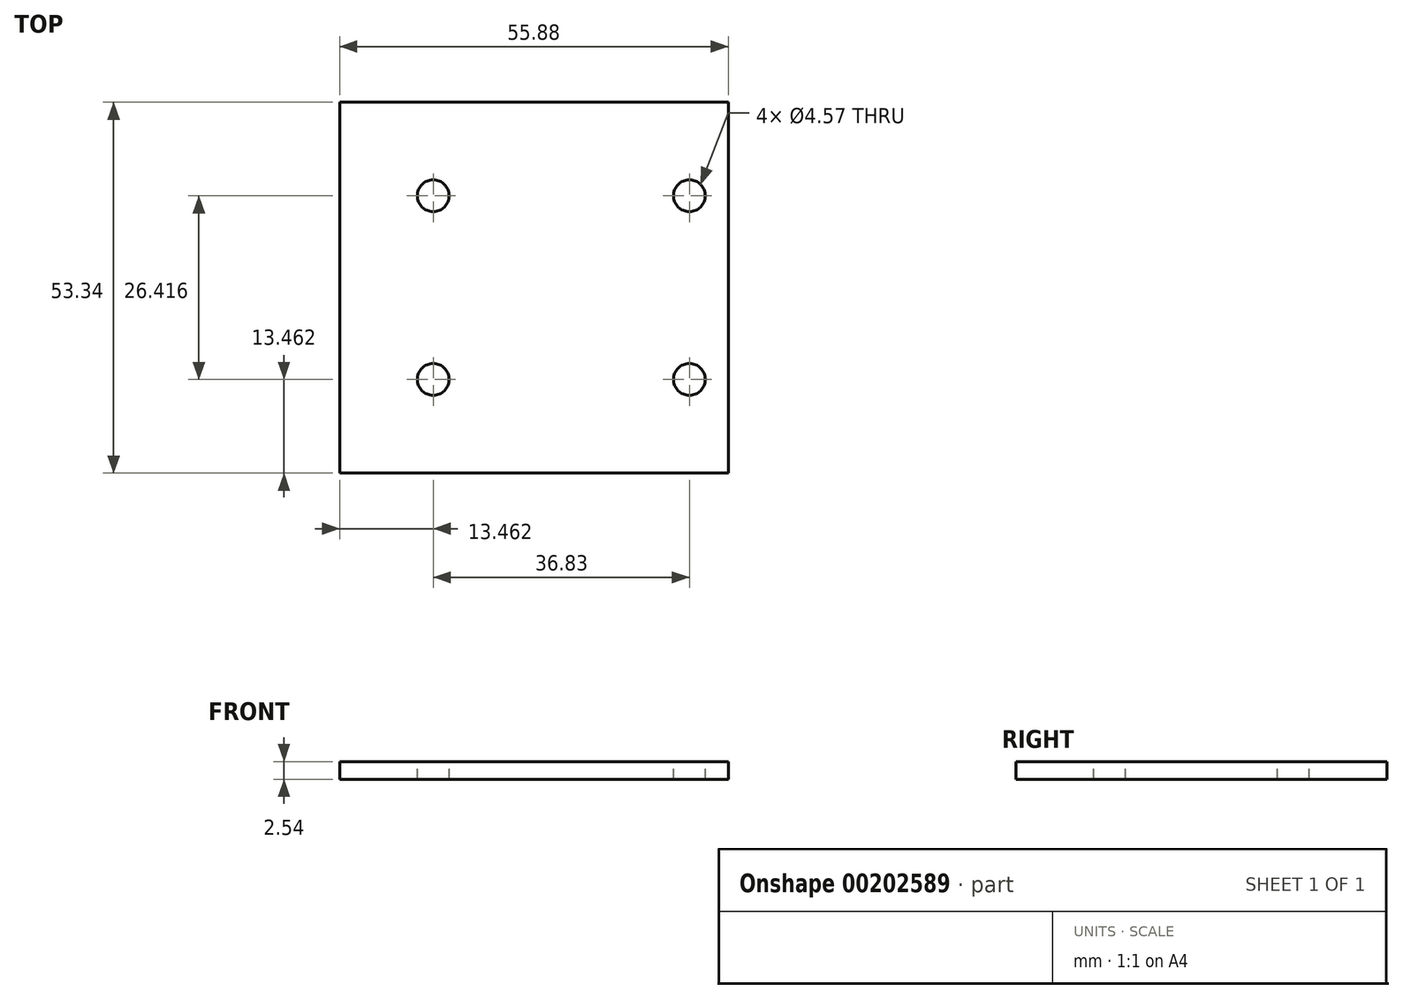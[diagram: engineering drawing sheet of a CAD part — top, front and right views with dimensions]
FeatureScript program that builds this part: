
annotation { "Feature Type Name" : "Feature", "Feature Type Description" : "" }
export const myFeature = defineFeature(function(context is Context, id is Id, definition is map)
    precondition{}
    {
        {
            var Q0;
            Q0=qCreatedBy(makeId("Top.planeOp"),FACE);
            var sketch = newSketch(context, id + "F0", { "sketchPlane" : qUnion([Q0])});
            skLineSegment(sketch, "E0.bottom", {"start": v(-27.94, 26.67) * mm, "end": v(27.94, 26.67) * mm});
            skLineSegment(sketch, "E0.top", {"start": v(-27.94, -26.67) * mm, "end": v(27.94, -26.67) * mm});
            skLineSegment(sketch, "E0.left", {"start": v(-27.94, 26.67) * mm, "end": v(-27.94, -26.67) * mm});
            skLineSegment(sketch, "E0.right", {"start": v(27.94, 26.67) * mm, "end": v(27.94, -26.67) * mm});
            skSolve(sketch);
        }
        {
            var Q0;
            Q0=makeQuery(id+"F0.imprint","IMPRINT",FACE,{"disambiguationData":[TD([[makeQuery(id+"F0.imprint","IMPRINT",EDGE,{"derivedFrom":sQuery(id+"F0.wireOp",EDGE,"E0.bottom")}),-1.0]])]});
            extrude(context, id + "F1", {"entities" : qUnion([Q0]), "depth" : 2.54 * mm});
        }
        {
            var Q0;
            Q0=makeQuery(id+"F1.opExtrude","CAP_FACE",FACE,{"disambiguationData":[OSD([sQuery(id+"F0.wireOp",EDGE,"E0.bottom"),sQuery(id+"F0.wireOp",EDGE,"E0.top"),sQuery(id+"F0.wireOp",EDGE,"E0.left"),sQuery(id+"F0.wireOp",EDGE,"E0.right")])],"isStart":false});
            var sketch = newSketch(context, id + "F2", { "sketchPlane" : qUnion([Q0])});
            skCircle(sketch, "E1", {"center": v(-14.48, 13.2) * mm, "radius": 2.29 * mm});
            skCircle(sketch, "E2", {"center": v(22.35, 13.2) * mm, "radius": 2.29 * mm});
            skCircle(sketch, "E3", {"center": v(-14.48, -13.2) * mm, "radius": 2.29 * mm});
            skCircle(sketch, "E4", {"center": v(22.35, -13.2) * mm, "radius": 2.29 * mm});
            skSolve(sketch);
        }
        {
            var Q0;
            Q0=sQuery(id+"F2.wireOp",VERTEX,"E1.center");
            var Q1;
            Q1=sQuery(id+"F2.wireOp",VERTEX,"E2.center");
            var Q2;
            Q2=sQuery(id+"F2.wireOp",VERTEX,"E3.center");
            var Q3;
            Q3=sQuery(id+"F2.wireOp",VERTEX,"E4.center");
            var Q4;
            Q4=makeQuery(id+"F1.opExtrude","SWEPT_BODY",BODY,{"disambiguationData":[OSD([sQuery(id+"F0.wireOp",EDGE,"E0.bottom"),sQuery(id+"F0.wireOp",EDGE,"E0.top"),sQuery(id+"F0.wireOp",EDGE,"E0.left"),sQuery(id+"F0.wireOp",EDGE,"E0.right")])]});
            hole(context, id + "F3", {"style" : HoleStyle.SIMPLE, "endStyle" : HoleEndStyle.THROUGH, "holeDiameter" : 4.57 * mm, "locations" : qUnion([Q0, Q1, Q2, Q3]), "scope" : qUnion([Q4]), "isTappedThrough" : true});
        }
    });
